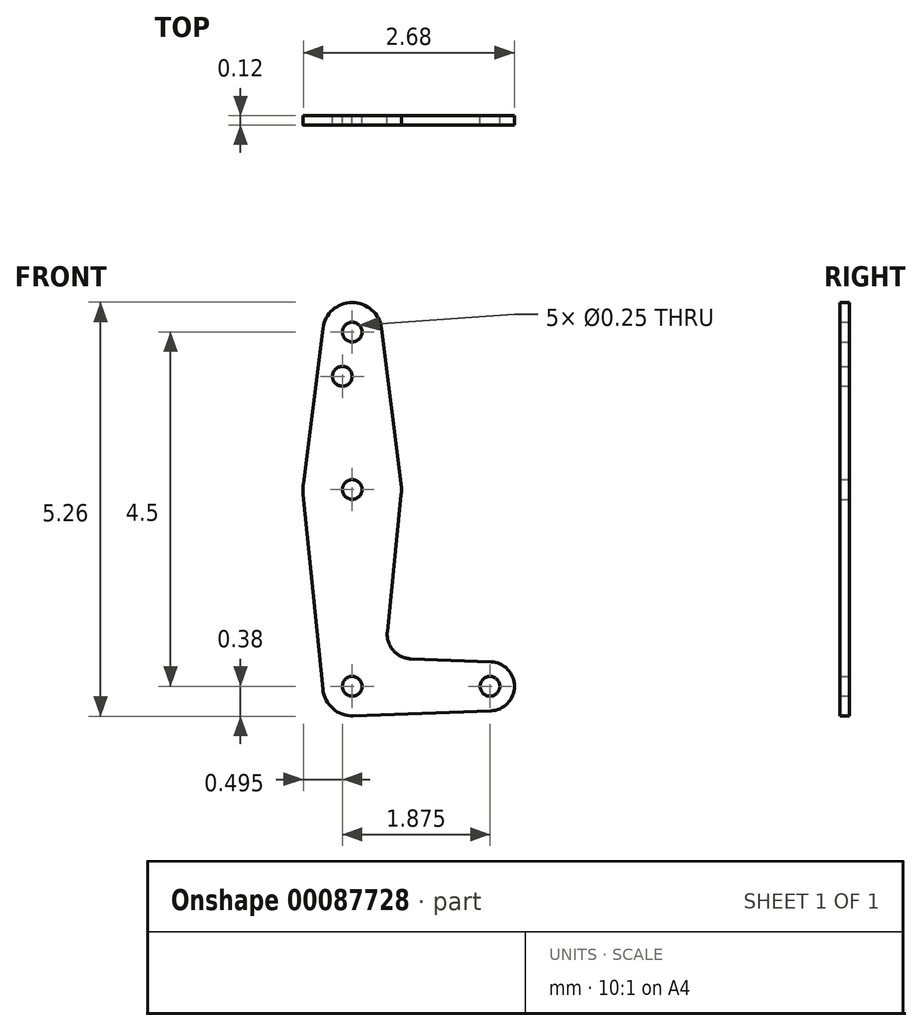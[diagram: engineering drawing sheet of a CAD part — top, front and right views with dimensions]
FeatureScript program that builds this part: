
annotation { "Feature Type Name" : "Feature", "Feature Type Description" : "" }
export const myFeature = defineFeature(function(context is Context, id is Id, definition is map)
    precondition{}
    {
        {
            var Q0;
            Q0=qCreatedBy(makeId("Front.planeOp"),FACE);
            var sketch = newSketch(context, id + "F0", { "sketchPlane" : qUnion([Q0])});
            skLineSegment(sketch, "E0", {"start": v(0, 4.5) * mm, "end": v(0, 0) * mm, "construction": true});
            skLineSegment(sketch, "E1", {"start": v(0, 0) * mm, "end": v(1.75, 0) * mm, "construction": true});
            skCircle(sketch, "E2", {"center": v(0, 4.5) * mm, "radius": 0.38 * mm});
            skCircle(sketch, "E3", {"center": v(0, 2.5) * mm, "radius": 0.63 * mm});
            skCircle(sketch, "E4", {"center": v(0, 0) * mm, "radius": 0.38 * mm});
            skCircle(sketch, "E5", {"center": v(1.75, 0) * mm, "radius": 0.31 * mm});
            skLineSegment(sketch, "E6", {"start": v(0.62, 2.44) * mm, "end": v(0.45, 0.7) * mm});
            skLineSegment(sketch, "E7", {"start": v(-0.62, 2.44) * mm, "end": v(-0.37, -0.04) * mm});
            skLineSegment(sketch, "E8", {"start": v(0.37, 4.55) * mm, "end": v(0.62, 2.58) * mm});
            skLineSegment(sketch, "E9", {"start": v(-0.37, 4.55) * mm, "end": v(-0.62, 2.58) * mm});
            skLineSegment(sketch, "E10", {"start": v(0.75, 0.35) * mm, "end": v(1.76, 0.31) * mm});
            skLineSegment(sketch, "E11", {"start": v(0.01, -0.37) * mm, "end": v(1.76, -0.31) * mm});
            skCircle(sketch, "E12", {"center": v(0, 4.5) * mm, "radius": 0.12 * mm});
            skCircle(sketch, "E13", {"center": v(-0.12, 3.94) * mm, "radius": 0.12 * mm});
            skCircle(sketch, "E14", {"center": v(0, 2.5) * mm, "radius": 0.12 * mm});
            skCircle(sketch, "E15", {"center": v(0, 0) * mm, "radius": 0.12 * mm});
            skCircle(sketch, "E16", {"center": v(1.75, 0) * mm, "radius": 0.12 * mm});
            skArc(sketch, "E17.filletArc", {"start": v(0.45, 0.7) * mm, "mid": v(0.52, 0.46) * mm, "end": v(0.75, 0.35) * mm});
            skSolve(sketch);
        }
        {
            var Q0;
            Q0 = qSketchRegion(id + "F0", true);
            extrude(context, id + "F1", {"entities" : qUnion([Q0]), "depth" : .12 * mm});
        }
    });
